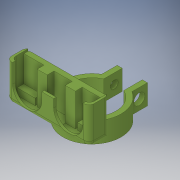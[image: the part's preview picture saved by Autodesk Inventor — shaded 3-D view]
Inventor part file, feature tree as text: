
AUTODESK INVENTOR PART (.ipt)
format: ipt  version: 2018 (Build 220112000, 112)  size: 330,752 bytes
history: native  units: in
note: dims shown in document units (in); Inventor stores cm internally (conversion verified against a paired STEP export)
features: extrude x8, sketch x8, fillet x3, reference x3, other x2, projected_geometry x1
ambient origin geometry x8: Origin, YZ Plane, XZ Plane, XY Plane, X Axis, Y Axis, Z Axis, Center Point
bodies: Solid1 (feature_tree)
feature tree (25):
  extrude  "Extrusion1"  Depth=0.125in
  extrude  "Extrusion2"  Depth=0.125in
  extrude  "Extrusion3"  Depth=0.125in
  extrude  "Extrusion4"  Depth=0.25in
  extrude  "Extrusion5"  Depth=0.194in
  extrude  "Extrusion7"  Depth=0.04in
  extrude  "Extrusion8"  Depth=0.8125in TaperAngle=0.0deg
  extrude  "Extrusion9"  Depth=0.125in
  fillet  "Fillet1"  Radius=0.05in
  fillet  "Fillet2"  Radius=0.05in
  fillet  "Fillet3"  Radius=0.05in
  sketch  "Sketch1"  dims[d0=1.19in d1=0.125in]
  sketch  "Sketch2"  dims[d2=0.125in d3=0.375in]
  sketch  "Sketch3"  dims[d4=1.0in d5=0.125in]
  sketch  "Sketch4"  dims[d6=0.5in d7=0.0in d8=0.25in]
  sketch  "Sketch5"  dims[d9=0.2in d10=0.194in]
  sketch  "Sketch7"  dims[d11=1.0in d12=0.0in d13=0.04in]
  projected_geometry  "Projected Loop3"
  sketch  "Sketch8"  dims[d14=1.0in d15=0.0in d18=0.8125in d19=0.0in]
  sketch  "Sketch9"  dims[d20=1.95in d21=0.975in d22=0.05in d23=0.05in d24=0.05in d25=0.05in d26=0.445in d27=0.0in d28=0.9125in d29=0.8in d30=0.05in d31=0.05in d35=0.17in d36=0.0in d37=0.25in d38=0.25in d39=0.5in d40=0.5in d41=0.17in d42=0.0in d43=0.05in d44=0.05in d45=0.0625in d46=0.0in d47=0.05in d48=0.125in d49=0.25in d50=0.125in]
  reference  "Reference1"
  reference  "Reference2"
  reference  "Reference3"
  other  "Assembly1"
  other  "Ultrasonic_sensor:1"
